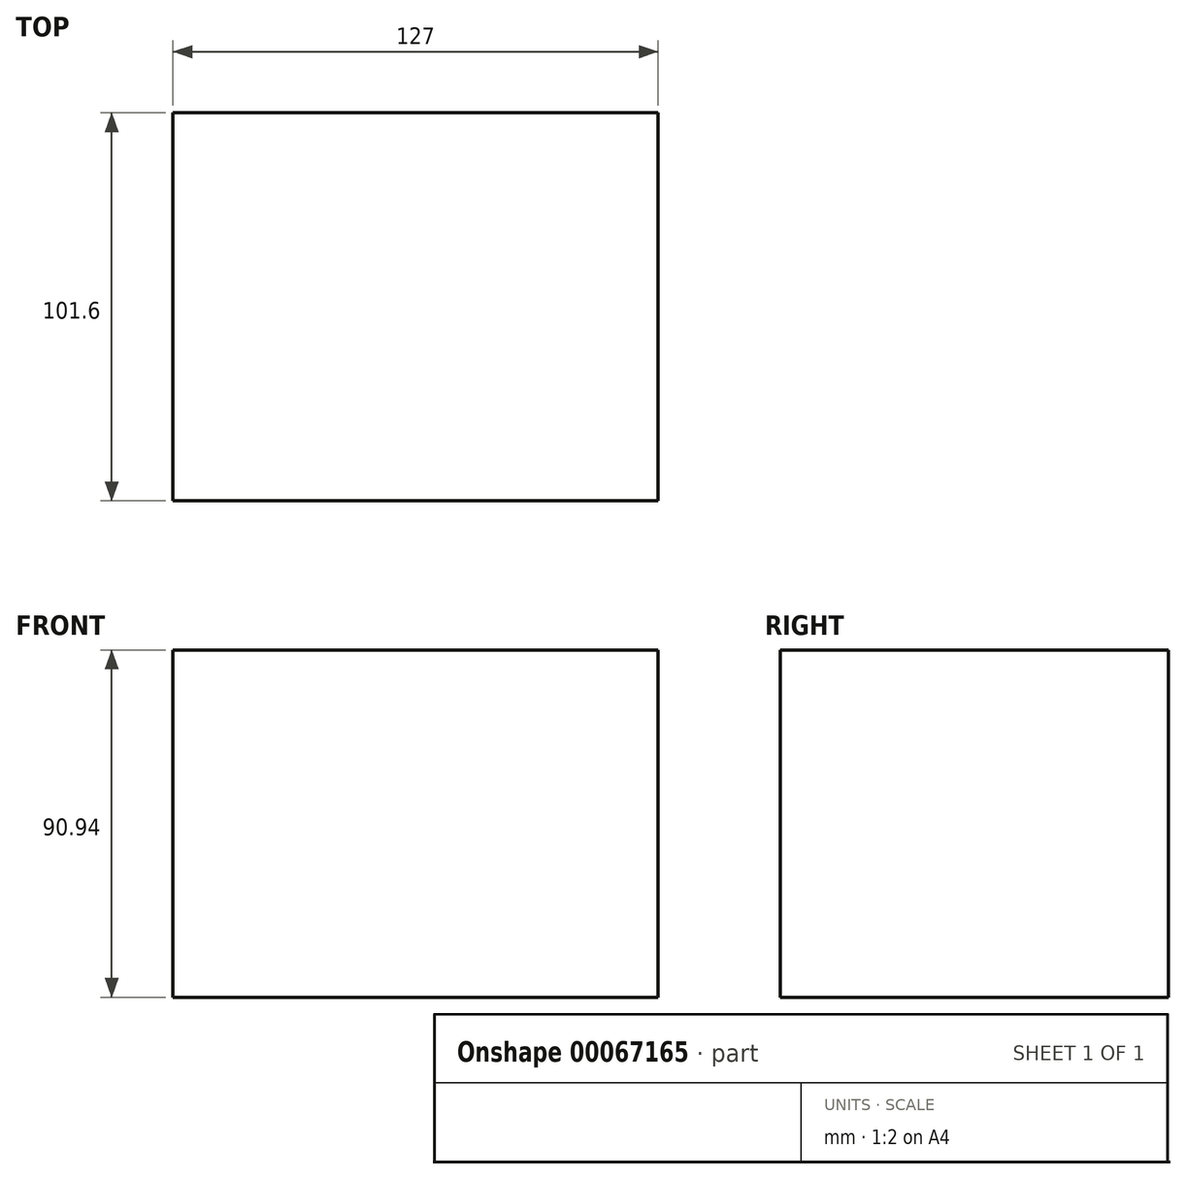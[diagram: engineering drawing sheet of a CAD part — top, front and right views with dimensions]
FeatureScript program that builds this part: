
annotation { "Feature Type Name" : "Feature", "Feature Type Description" : "" }
export const myFeature = defineFeature(function(context is Context, id is Id, definition is map)
    precondition{}
    {
        {
            var Q0;
            Q0=qCreatedBy(makeId("Top.planeOp"),FACE);
            var sketch = newSketch(context, id + "F0", { "sketchPlane" : qUnion([Q0])});
            skLineSegment(sketch, "E0.bottom", {"start": v(-64.32, 52.92) * mm, "end": v(62.68, 52.92) * mm});
            skLineSegment(sketch, "E0.top", {"start": v(-64.32, -48.68) * mm, "end": v(62.68, -48.68) * mm});
            skLineSegment(sketch, "E0.left", {"start": v(-64.32, 52.92) * mm, "end": v(-64.32, -48.68) * mm});
            skLineSegment(sketch, "E0.right", {"start": v(62.68, 52.92) * mm, "end": v(62.68, -48.68) * mm});
            skSolve(sketch);
        }
        {
            var Q0;
            Q0 = qSketchRegion(id + "F0", true);
            extrude(context, id + "F1", {"entities" : qUnion([Q0]), "oppositeDirection" : true, "depth" : 47.17 * mm, "hasSecondDirection" : true, "secondDirectionOppositeDirection" : false, "secondDirectionDepth" : 43.77 * mm});
        }
    });
